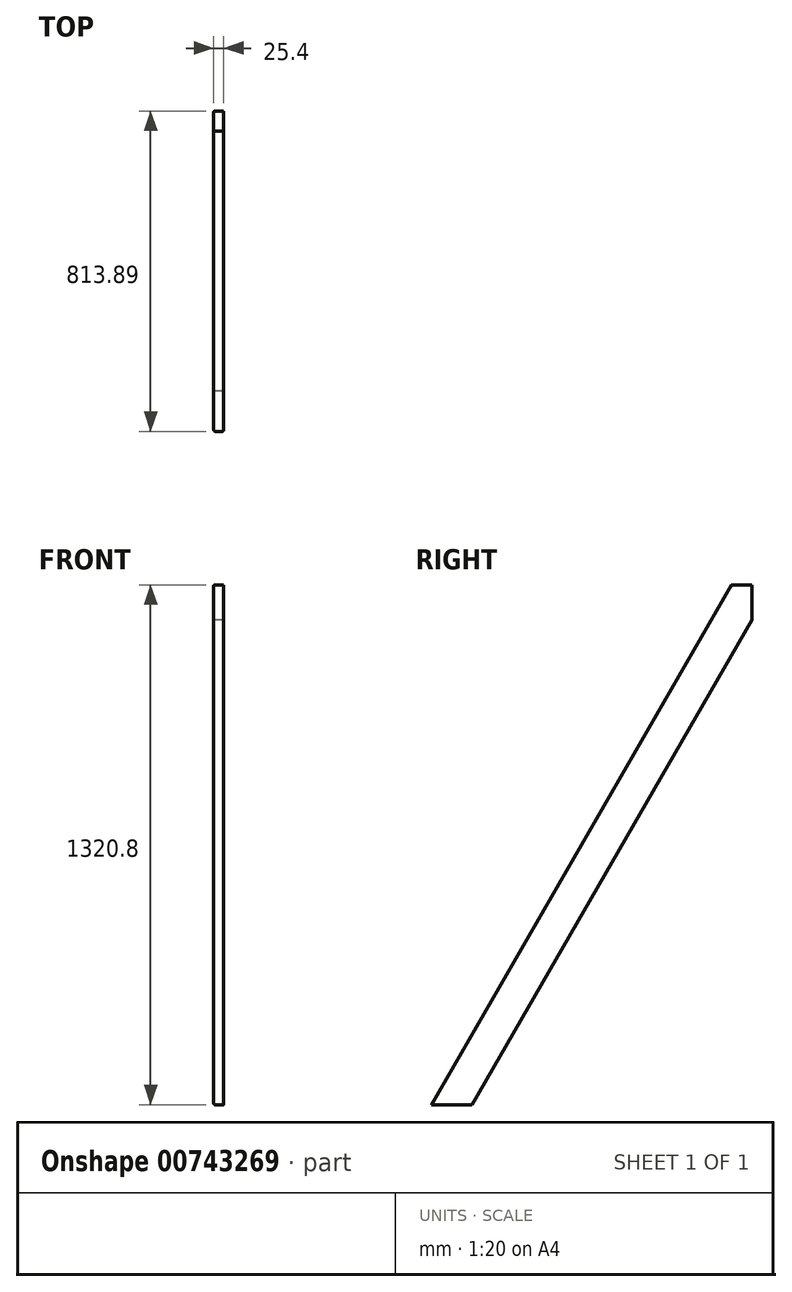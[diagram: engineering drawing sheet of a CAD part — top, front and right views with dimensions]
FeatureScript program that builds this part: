
annotation { "Feature Type Name" : "Feature", "Feature Type Description" : "" }
export const myFeature = defineFeature(function(context is Context, id is Id, definition is map)
    precondition{}
    {
        {
            var Q0;
            Q0=qCreatedBy(makeId("Right.planeOp"),FACE);
            var sketch = newSketch(context, id + "F0", { "sketchPlane" : qUnion([Q0])});
            skLineSegment(sketch, "E0", {"start": v(0, 0) * mm, "end": v(762.56, 1320.8) * mm});
            skLineSegment(sketch, "E1", {"start": v(762.56, 1320.8) * mm, "end": v(813.9, 1320.8) * mm});
            skLineSegment(sketch, "E2", {"start": v(813.9, 1231.9) * mm, "end": v(102.65, 0) * mm});
            skLineSegment(sketch, "E3", {"start": v(0, 0) * mm, "end": v(102.65, 0) * mm});
            skLineSegment(sketch, "E4", {"start": v(813.9, 1320.8) * mm, "end": v(813.9, 1231.9) * mm});
            skSolve(sketch);
        }
        {
            var Q0;
            Q0 = qSketchRegion(id + "F0", true);
            extrude(context, id + "F1", {"entities" : qUnion([Q0]), "depth" : 25.4 * mm, "offsetDistance" : 25.4 * mm});
        }
        {
            var Q0;
            Q0=makeQuery(id+"F1.opExtrude","CAP_EDGE",EDGE,{"disambiguationData":[OSD([sQuery(id+"F0.wireOp",EDGE,"E0")])],"isStart":false});
            var Q1;
            Q1=makeQuery(id+"F1.opExtrude","CAP_EDGE",EDGE,{"disambiguationData":[OSD([sQuery(id+"F0.wireOp",EDGE,"E0")])],"isStart":true});
            var Q2;
            Q2=makeQuery(id+"F1.opExtrude","CAP_FACE",FACE,{"disambiguationData":[OSD([sQuery(id+"F0.wireOp",EDGE,"E0"),sQuery(id+"F0.wireOp",EDGE,"E1"),sQuery(id+"F0.wireOp",EDGE,"E2"),sQuery(id+"F0.wireOp",EDGE,"E3"),sQuery(id+"F0.wireOp",EDGE,"E4")])],"isStart":true});
            var Q3;
            Q3=makeQuery(id+"F1.opExtrude","CAP_EDGE",EDGE,{"disambiguationData":[OSD([sQuery(id+"F0.wireOp",EDGE,"E2")])],"isStart":false});
            var Q4;
            Q4=makeQuery(id+"F1.opExtrude","CAP_EDGE",EDGE,{"disambiguationData":[OSD([sQuery(id+"F0.wireOp",EDGE,"E2")])],"isStart":true});
            fillet(context, id + "F2", {"entities" : qUnion([Q0, Q1, Q2, Q3, Q4]), "radius" : 3.17 * mm, "tangentPropagation" : true, "allowEdgeOverflow" : false});
        }
    });
